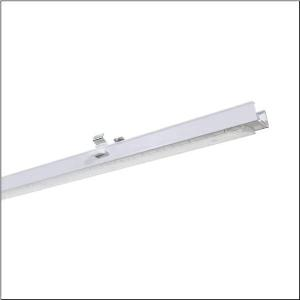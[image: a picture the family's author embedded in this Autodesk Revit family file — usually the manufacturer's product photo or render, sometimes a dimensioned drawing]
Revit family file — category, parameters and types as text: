
# Revit family: trunking_flex_31_51re12ma16b
name_source: partatom
category: Lighting Fixtures
units: mm (PartAtom-declared; Revit-internal decimal feet)

## family parameters
Cut with Voids When Loaded = No
Host = Face
Light Source = No
Part Type = Normal
Room Calculation Point = No
Round Connector Dimension = Use Diameter
Shared = No

## types (1)
- --- (1 x LED, 6400 lm, 40 W, 3500K)
    Apparent Load = 40 VA
    CIE Flux Codes = 65 91 98 99 100
    Color Rendering = 80
    Color Temperature = 3500K
    Default Elevation = 1800 mm
    Description = Trunking Flex 31, luminaire insert, of extruded aluminium section, coated, traffic white (RAL 9016), length: 1.172mm, width: 91mm, height: 53mm, LED rated luminous flux: 6.400lm, light colour: 835, control gear: ON/OFF Multilumen, with system connector: socket, mains connection: 220..240V, AC, 50/60Hz, rated input power: 40W, luminous flux adjustable on luminaire in four steps (3420/4540/5580/6630lm), connected load according to luminous flux setting (20/26/33/40W), primary light control with lens, of plastic, primary optical cover: cover, of PMMA, light emission: direct distribution, protection rating (complete): IP20, insulation class (complete): insulation class I (protective earthing), certification: CE, UKCA, impact resistance: IK02, permissible ambient temperature for indoor applications: -20..+40°C, packaging unit: 1 piece
    Height = 58 mm
    Lamp = 1 x LED
    Lamp Light Flux = 6400 lm
    Lamp Power = 40 W
    Lamp count = 1
    Length = 1172 mm
    Luminous efficacy = 160 lm/W
    Manufacturer = Siteco
    ModVariant = No
    Model = 51RE12MA16B
    Mounting Place = Ceiling
    Mounting Type = Pendant
    Number of Poles = 1
    OnlyDefault = Yes
    Power Factor = 1
    Product Name = Trunking Flex 31
    Product group = luminaire insert
    ProductGroupID = 901
    Protection Class = Protection class I
    Protection Degree = IP 20
    RLX_Detail_Level = 1
    RLX_Emergency_Light_Flux = 0 lm
    RLX_Emergency_Type = 0
    RLX_Emergency_Type_DB = No
    RlxData = <blob elided: 19957 chars, md5=40927baa>
    Socket = socket
    Standby Power = 0 W
    System Light Flux = 6400 lm
    System Power = 40 W
    Type Comments = factory setting: luminous flux: 100 % | (ON | ON) | 300 mA
    Type Image = l_1266702.jpg
    URL = http://relux.com
    VarID = @adj_001305
    Voltage = 0 V
    Weight = 0.00 kg
    Width = 65 mm

## geometry (parser evidence)
native form markers: Blend x4, Sweep x11
no freeform markers — native parametric forms only
